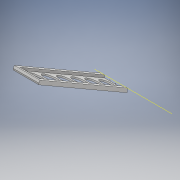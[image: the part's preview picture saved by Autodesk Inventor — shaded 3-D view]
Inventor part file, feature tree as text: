
AUTODESK INVENTOR PART (.ipt)
format: ipt  version: 2018 (Build 220112000, 112)  size: 301,568 bytes
history: native  units: mm
features: extrude x13, sketch x7, plane x4, other x2, mirror x2, projected_geometry x1
ambient origin geometry x8: Origin, YZ Plane, XZ Plane, XY Plane, X Axis, Y Axis, Z Axis, Center Point
bodies: Body1 (feature_tree)
feature tree (29):
  other  "Sólido1"
  sketch  "Boceto1"  dims[d7=5.0mm d9=2.5mm d10=0.0mm]
  extrude  "Extrusión1"  Depth=5.0mm TaperAngle=0.0deg
  extrude  "Extrusión2"  Depth=5.0mm
  plane  "Plano de trabajo3"
  mirror  "Simetría3"
  extrude  "Extrusión11"  Depth=5.0mm
  sketch  "Boceto7"  dims[d69=33.5mm d74=5.0mm]
  plane  "Plano de trabajo4"
  extrude  "Extrusión12"  Depth=5.0mm
  extrude  "Extrusión13"  Depth=8.0mm
  extrude  "Extrusión14"  Depth=42.4mm
  mirror  "Simetría4"
  extrude  "Extrusión15"  Depth=2.6mm TaperAngle=0.0deg
  sketch  "Boceto9"  dims[d77=70.0mm d78=8.0mm]
  other  "Eje de trabajo2"
  extrude  "Extrusión16"  TaperAngle=120.0deg  [1 undecoded]
  plane  "Plano de trabajo5"
  plane  "Plano de trabajo6"
  sketch  "Boceto11"  dims[d79=4.5mm d80=0.0mm d81=42.4mm]
  extrude  "Extrusión18"  Depth=5.0mm TaperAngle=0.0deg
  extrude  "Extrusión19"  Depth=2.6mm TaperAngle=0.0deg
  extrude  "Extrusión20"  Depth=5.0mm
  extrude  "Extrusión21"  Depth=2.6mm
  extrude  "Extrusión22"  Depth=5.0mm
  sketch  "Boceto6"  dims[d11=1.0mm d12=0.0mm d68=5.0mm]
  sketch  "Boceto8"  dims[d75=33.5mm d76=5.0mm]
  projected_geometry  "Contorno proyectado2"
  sketch  "Boceto12"  dims[d82=173.0mm d86=21.75mm d87=0.0mm d88=120.0deg d89=5.0mm d90=0.0mm d92=21.75mm d93=0.0mm d94=5.0mm d95=20.5mm d96=5.0mm d97=5.0mm d98=5.0mm d99=5.0mm d100=5.0mm d101=22.0mm d102=22.38mm d103=23.0mm d104=24.38mm d105=25.5mm d106=21.75mm d107=0.0mm d108=5.0mm d109=2.5mm d110=40.0mm d111=30.0mm d112=31.5mm d113=21.75mm d114=0.0mm d117=2.5mm d118=2.5mm d119=38.5mm d120=1.5mm d121=1.5mm d122=1.5mm d123=10.0mm d124=10.0mm d126=2.5mm d127=0.0mm d128=2.5mm d129=0.0mm d130=10.0mm d131=0.0mm d132=2.4mm d133=0.0mm d134=2.6mm d135=0.0mm]
note: 1 required parameter value undecoded (feature->parameter linkage not recoverable at this tier; creation-order binding heuristic only, values carry confidence <= 0.55)
